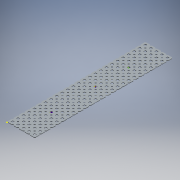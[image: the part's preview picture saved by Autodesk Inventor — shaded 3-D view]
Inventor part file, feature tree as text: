
AUTODESK INVENTOR PART (.ipt)
format: ipt  version: 2018 (Build 220112000, 112)  size: 2,300,416 bytes
history: native  units: mm (DEFAULTED — no unit token found)
features: other x125, extrude x125, sketch x4, imported_body x1, pattern_linear x1
ambient origin geometry x8: Origin, YZ Plane, XZ Plane, XY Plane, X Axis, Y Axis, Z Axis, Center Point
bodies: Solid1 (feature_tree)
feature tree (256):
  imported_body  "Base1"
  pattern_linear  "Rectangular Pattern1"  Count1=25  [1 undecoded]
  sketch  "Sketch2"  dims[d2=0.0mm d3=250.0mm]
  sketch  "Sketch3"  dims[d5=12.7mm d6=50.0mm d8=12.7mm]
  sketch  "Sketch4"  dims[d9=0.0mm d10=0.0mm d11=0.0mm d12=0.0mm d13=0.0mm d14=0.0mm d15=0.0mm d16=0.0mm d17=0.0mm d18=0.0mm d19=0.0mm d20=0.0mm d21=0.0mm d22=0.0mm d23=0.0mm d24=0.0mm d25=0.0mm d26=0.0mm d27=0.0mm d28=0.0mm d29=0.0mm d30=0.0mm d31=0.0mm d32=0.0mm d33=0.0mm d34=0.0mm d35=0.0mm d36=0.0mm d37=0.0mm d38=0.0mm d39=0.0mm d40=0.0mm d41=0.0mm d42=0.0mm d43=0.0mm d44=0.0mm d45=0.0mm d46=0.0mm d47=0.0mm d48=0.0mm d49=0.0mm d50=0.0mm d51=0.0mm d52=0.0mm d53=0.0mm d54=0.0mm d55=0.0mm d56=0.0mm d57=0.0mm d58=0.0mm d59=0.0mm d60=0.0mm d61=0.0mm d62=0.0mm d63=0.0mm d64=0.0mm d65=0.0mm d66=0.0mm d67=0.0mm d68=0.0mm d69=0.0mm d70=0.0mm d71=0.0mm d72=0.0mm d73=0.0mm d74=0.0mm d75=0.0mm d76=0.0mm d77=0.0mm d78=0.0mm d79=0.0mm d80=0.0mm d81=0.0mm d82=0.0mm d83=0.0mm d84=0.0mm d85=0.0mm d86=0.0mm d87=0.0mm d88=0.0mm d89=0.0mm d90=0.0mm d91=0.0mm d92=0.0mm d93=0.0mm d94=0.0mm d95=0.0mm d96=0.0mm d97=0.0mm d98=0.0mm d99=0.0mm d100=0.0mm d101=0.0mm d102=0.0mm d103=0.0mm d104=0.0mm d105=0.0mm d106=0.0mm d107=0.0mm d108=0.0mm d109=0.0mm d110=0.0mm d111=0.0mm d112=0.0mm d113=0.0mm d114=0.0mm d115=0.0mm d116=0.0mm d117=0.0mm d118=0.0mm d119=0.0mm d120=0.0mm d121=0.0mm d122=0.0mm d123=0.0mm d124=0.0mm d125=0.0mm d126=0.0mm d127=0.0mm d128=0.0mm d129=0.0mm d130=0.0mm d131=0.0mm d132=0.0mm d133=0.0mm d134=0.0mm d135=0.0mm d136=0.0mm d137=0.0mm d138=0.0mm d139=0.0mm d140=0.0mm d141=0.0mm d142=0.0mm d143=0.0mm d144=0.0mm d145=0.0mm d146=0.0mm d147=0.0mm d148=0.0mm d149=0.0mm d150=0.0mm d151=0.0mm d152=0.0mm d153=0.0mm d154=0.0mm d155=0.0mm d156=0.0mm d157=0.0mm d158=0.0mm d159=0.0mm d160=0.0mm d161=0.0mm d162=0.0mm d163=0.0mm d164=0.0mm d165=0.0mm d166=0.0mm d167=0.0mm d168=0.0mm d169=0.0mm d170=0.0mm d171=0.0mm d172=0.0mm d173=0.0mm d174=0.0mm d175=0.0mm d176=0.0mm d177=0.0mm d178=0.0mm d179=0.0mm d180=0.0mm d181=0.0mm d182=0.0mm d183=0.0mm d184=0.0mm d185=0.0mm d186=0.0mm d187=0.0mm d188=0.0mm d189=0.0mm d190=0.0mm d191=0.0mm d192=0.0mm d193=0.0mm d194=0.0mm d195=0.0mm d196=0.0mm d197=0.0mm d198=0.0mm d199=0.0mm d200=0.0mm d201=0.0mm d202=0.0mm d203=0.0mm d204=0.0mm d205=0.0mm d206=0.0mm d207=0.0mm d208=0.0mm d209=0.0mm d210=0.0mm d211=0.0mm d212=0.0mm d213=0.0mm d214=0.0mm d215=0.0mm d216=0.0mm d217=0.0mm d218=0.0mm d219=0.0mm d220=0.0mm d221=0.0mm d222=0.0mm d223=0.0mm d224=0.0mm d225=0.0mm d226=0.0mm d227=0.0mm d228=0.0mm d229=0.0mm d230=0.0mm d231=0.0mm d232=0.0mm d233=0.0mm d234=0.0mm d235=0.0mm d236=0.0mm d237=0.0mm d238=0.0mm d239=0.0mm d240=0.0mm d241=0.0mm d242=0.0mm d243=0.0mm d244=0.0mm d245=0.0mm d246=0.0mm d247=0.0mm d248=0.0mm d249=0.0mm d250=0.0mm d251=0.0mm d252=0.0mm d253=0.0mm d254=0.0mm d255=0.0mm d256=0.0mm d257=0.0mm d258=0.0mm]
  sketch  "Sketch1"  dims[d1=1.1684mm]
  other  "Srf1"
  other  "Srf2"
  other  "Srf3"
  other  "Srf4"
  other  "Srf5"
  other  "Srf6"
  other  "Srf7"
  other  "Srf8"
  other  "Srf9"
  other  "Srf10"
  other  "Srf11"
  other  "Srf12"
  other  "Srf13"
  other  "Srf14"
  other  "Srf15"
  other  "Srf16"
  other  "Srf17"
  other  "Srf18"
  other  "Srf19"
  other  "Srf20"
  other  "Srf21"
  other  "Srf22"
  other  "Srf23"
  other  "Srf24"
  other  "Srf25"
  other  "Srf26"
  other  "Srf27"
  other  "Srf28"
  other  "Srf29"
  other  "Srf30"
  other  "Srf31"
  other  "Srf32"
  other  "Srf33"
  other  "Srf34"
  other  "Srf35"
  other  "Srf36"
  other  "Srf37"
  other  "Srf38"
  other  "Srf39"
  other  "Srf40"
  other  "Srf41"
  other  "Srf42"
  other  "Srf43"
  other  "Srf44"
  other  "Srf45"
  other  "Srf46"
  other  "Srf47"
  other  "Srf48"
  other  "Srf49"
  other  "Srf50"
  other  "Srf51"
  other  "Srf52"
  other  "Srf53"
  other  "Srf54"
  other  "Srf55"
  other  "Srf56"
  other  "Srf57"
  other  "Srf58"
  other  "Srf59"
  other  "Srf60"
  other  "Srf61"
  other  "Srf62"
  other  "Srf63"
  other  "Srf64"
  other  "Srf65"
  other  "Srf66"
  other  "Srf67"
  other  "Srf68"
  other  "Srf69"
  other  "Srf70"
  other  "Srf71"
  other  "Srf72"
  other  "Srf73"
  other  "Srf74"
  other  "Srf75"
  other  "Srf76"
  other  "Srf77"
  other  "Srf78"
  other  "Srf79"
  other  "Srf80"
  other  "Srf81"
  other  "Srf82"
  other  "Srf83"
  other  "Srf84"
  other  "Srf85"
  other  "Srf86"
  other  "Srf87"
  other  "Srf88"
  other  "Srf89"
  other  "Srf90"
  other  "Srf91"
  other  "Srf92"
  other  "Srf93"
  other  "Srf94"
  other  "Srf95"
  other  "Srf96"
  other  "Srf97"
  other  "Srf98"
  other  "Srf99"
  other  "Srf100"
  other  "Srf101"
  other  "Srf102"
  other  "Srf103"
  other  "Srf104"
  other  "Srf105"
  other  "Srf106"
  other  "Srf107"
  other  "Srf108"
  other  "Srf109"
  other  "Srf110"
  other  "Srf111"
  other  "Srf112"
  other  "Srf113"
  other  "Srf114"
  other  "Srf115"
  other  "Srf116"
  other  "Srf117"
  other  "Srf118"
  other  "Srf119"
  other  "Srf120"
  other  "Srf121"
  other  "Srf122"
  other  "Srf123"
  other  "Srf124"
  other  "Srf125"
  extrude  "ExtrusionSrf1"  Depth=50.0mm
  extrude  "ExtrusionSrf2"  TaperAngle=0.0deg  [1 undecoded]
  extrude  "ExtrusionSrf3"  TaperAngle=0.0deg  [1 undecoded]
  extrude  "ExtrusionSrf4"  TaperAngle=0.0deg  [1 undecoded]
  extrude  "ExtrusionSrf5"  TaperAngle=0.0deg  [1 undecoded]
  extrude  "ExtrusionSrf6"  TaperAngle=0.0deg  [1 undecoded]
  extrude  "ExtrusionSrf7"  TaperAngle=0.0deg  [1 undecoded]
  extrude  "ExtrusionSrf8"  TaperAngle=0.0deg  [1 undecoded]
  extrude  "ExtrusionSrf9"  TaperAngle=0.0deg  [1 undecoded]
  extrude  "ExtrusionSrf10"  TaperAngle=0.0deg  [1 undecoded]
  extrude  "ExtrusionSrf11"  TaperAngle=0.0deg  [1 undecoded]
  extrude  "ExtrusionSrf12"  TaperAngle=0.0deg  [1 undecoded]
  extrude  "ExtrusionSrf13"  TaperAngle=0.0deg  [1 undecoded]
  extrude  "ExtrusionSrf14"  TaperAngle=0.0deg  [1 undecoded]
  extrude  "ExtrusionSrf15"  TaperAngle=0.0deg  [1 undecoded]
  extrude  "ExtrusionSrf16"  TaperAngle=0.0deg  [1 undecoded]
  extrude  "ExtrusionSrf17"  TaperAngle=0.0deg  [1 undecoded]
  extrude  "ExtrusionSrf18"  TaperAngle=0.0deg  [1 undecoded]
  extrude  "ExtrusionSrf19"  TaperAngle=0.0deg  [1 undecoded]
  extrude  "ExtrusionSrf20"  TaperAngle=0.0deg  [1 undecoded]
  extrude  "ExtrusionSrf21"  TaperAngle=0.0deg  [1 undecoded]
  extrude  "ExtrusionSrf22"  TaperAngle=0.0deg  [1 undecoded]
  extrude  "ExtrusionSrf23"  TaperAngle=0.0deg  [1 undecoded]
  extrude  "ExtrusionSrf24"  TaperAngle=0.0deg  [1 undecoded]
  extrude  "ExtrusionSrf25"  TaperAngle=0.0deg  [1 undecoded]
  extrude  "ExtrusionSrf26"  TaperAngle=0.0deg  [1 undecoded]
  extrude  "ExtrusionSrf27"  TaperAngle=0.0deg  [1 undecoded]
  extrude  "ExtrusionSrf28"  TaperAngle=0.0deg  [1 undecoded]
  extrude  "ExtrusionSrf29"  TaperAngle=0.0deg  [1 undecoded]
  extrude  "ExtrusionSrf30"  TaperAngle=0.0deg  [1 undecoded]
  extrude  "ExtrusionSrf31"  TaperAngle=0.0deg  [1 undecoded]
  extrude  "ExtrusionSrf32"  TaperAngle=0.0deg  [1 undecoded]
  extrude  "ExtrusionSrf33"  TaperAngle=0.0deg  [1 undecoded]
  extrude  "ExtrusionSrf34"  TaperAngle=0.0deg  [1 undecoded]
  extrude  "ExtrusionSrf35"  TaperAngle=0.0deg  [1 undecoded]
  extrude  "ExtrusionSrf36"  TaperAngle=0.0deg  [1 undecoded]
  extrude  "ExtrusionSrf37"  TaperAngle=0.0deg  [1 undecoded]
  extrude  "ExtrusionSrf38"  TaperAngle=0.0deg  [1 undecoded]
  extrude  "ExtrusionSrf39"  TaperAngle=0.0deg  [1 undecoded]
  extrude  "ExtrusionSrf40"  TaperAngle=0.0deg  [1 undecoded]
  extrude  "ExtrusionSrf41"  TaperAngle=0.0deg  [1 undecoded]
  extrude  "ExtrusionSrf42"  TaperAngle=0.0deg  [1 undecoded]
  extrude  "ExtrusionSrf43"  TaperAngle=0.0deg  [1 undecoded]
  extrude  "ExtrusionSrf44"  TaperAngle=0.0deg  [1 undecoded]
  extrude  "ExtrusionSrf45"  TaperAngle=0.0deg  [1 undecoded]
  extrude  "ExtrusionSrf46"  TaperAngle=0.0deg  [1 undecoded]
  extrude  "ExtrusionSrf47"  TaperAngle=0.0deg  [1 undecoded]
  extrude  "ExtrusionSrf48"  TaperAngle=0.0deg  [1 undecoded]
  extrude  "ExtrusionSrf49"  TaperAngle=0.0deg  [1 undecoded]
  extrude  "ExtrusionSrf50"  TaperAngle=0.0deg  [1 undecoded]
  extrude  "ExtrusionSrf51"  TaperAngle=0.0deg  [1 undecoded]
  extrude  "ExtrusionSrf52"  TaperAngle=0.0deg  [1 undecoded]
  extrude  "ExtrusionSrf53"  TaperAngle=0.0deg  [1 undecoded]
  extrude  "ExtrusionSrf54"  TaperAngle=0.0deg  [1 undecoded]
  extrude  "ExtrusionSrf55"  TaperAngle=0.0deg  [1 undecoded]
  extrude  "ExtrusionSrf56"  TaperAngle=0.0deg  [1 undecoded]
  extrude  "ExtrusionSrf57"  TaperAngle=0.0deg  [1 undecoded]
  extrude  "ExtrusionSrf58"  TaperAngle=0.0deg  [1 undecoded]
  extrude  "ExtrusionSrf59"  TaperAngle=0.0deg  [1 undecoded]
  extrude  "ExtrusionSrf60"  TaperAngle=0.0deg  [1 undecoded]
  extrude  "ExtrusionSrf61"  TaperAngle=0.0deg  [1 undecoded]
  extrude  "ExtrusionSrf62"  TaperAngle=0.0deg  [1 undecoded]
  extrude  "ExtrusionSrf63"  TaperAngle=0.0deg  [1 undecoded]
  extrude  "ExtrusionSrf64"  TaperAngle=0.0deg  [1 undecoded]
  extrude  "ExtrusionSrf65"  TaperAngle=0.0deg  [1 undecoded]
  extrude  "ExtrusionSrf66"  TaperAngle=0.0deg  [1 undecoded]
  extrude  "ExtrusionSrf67"  TaperAngle=0.0deg  [1 undecoded]
  extrude  "ExtrusionSrf68"  TaperAngle=0.0deg  [1 undecoded]
  extrude  "ExtrusionSrf69"  TaperAngle=0.0deg  [1 undecoded]
  extrude  "ExtrusionSrf70"  TaperAngle=0.0deg  [1 undecoded]
  extrude  "ExtrusionSrf71"  TaperAngle=0.0deg  [1 undecoded]
  extrude  "ExtrusionSrf72"  TaperAngle=0.0deg  [1 undecoded]
  extrude  "ExtrusionSrf73"  TaperAngle=0.0deg  [1 undecoded]
  extrude  "ExtrusionSrf74"  TaperAngle=0.0deg  [1 undecoded]
  extrude  "ExtrusionSrf75"  TaperAngle=0.0deg  [1 undecoded]
  extrude  "ExtrusionSrf76"  TaperAngle=0.0deg  [1 undecoded]
  extrude  "ExtrusionSrf77"  TaperAngle=0.0deg  [1 undecoded]
  extrude  "ExtrusionSrf78"  TaperAngle=0.0deg  [1 undecoded]
  extrude  "ExtrusionSrf79"  TaperAngle=0.0deg  [1 undecoded]
  extrude  "ExtrusionSrf80"  TaperAngle=0.0deg  [1 undecoded]
  extrude  "ExtrusionSrf81"  TaperAngle=0.0deg  [1 undecoded]
  extrude  "ExtrusionSrf82"  TaperAngle=0.0deg  [1 undecoded]
  extrude  "ExtrusionSrf83"  TaperAngle=0.0deg  [1 undecoded]
  extrude  "ExtrusionSrf84"  TaperAngle=0.0deg  [1 undecoded]
  extrude  "ExtrusionSrf85"  TaperAngle=0.0deg  [1 undecoded]
  extrude  "ExtrusionSrf86"  TaperAngle=0.0deg  [1 undecoded]
  extrude  "ExtrusionSrf87"  TaperAngle=0.0deg  [1 undecoded]
  extrude  "ExtrusionSrf88"  TaperAngle=0.0deg  [1 undecoded]
  extrude  "ExtrusionSrf89"  TaperAngle=0.0deg  [1 undecoded]
  extrude  "ExtrusionSrf90"  TaperAngle=0.0deg  [1 undecoded]
  extrude  "ExtrusionSrf91"  TaperAngle=0.0deg  [1 undecoded]
  extrude  "ExtrusionSrf92"  TaperAngle=0.0deg  [1 undecoded]
  extrude  "ExtrusionSrf93"  TaperAngle=0.0deg  [1 undecoded]
  extrude  "ExtrusionSrf94"  TaperAngle=0.0deg  [1 undecoded]
  extrude  "ExtrusionSrf95"  TaperAngle=0.0deg  [1 undecoded]
  extrude  "ExtrusionSrf96"  TaperAngle=0.0deg  [1 undecoded]
  extrude  "ExtrusionSrf97"  TaperAngle=0.0deg  [1 undecoded]
  extrude  "ExtrusionSrf98"  TaperAngle=0.0deg  [1 undecoded]
  extrude  "ExtrusionSrf99"  TaperAngle=0.0deg  [1 undecoded]
  extrude  "ExtrusionSrf100"  TaperAngle=0.0deg  [1 undecoded]
  extrude  "ExtrusionSrf101"  TaperAngle=0.0deg  [1 undecoded]
  extrude  "ExtrusionSrf102"  TaperAngle=0.0deg  [1 undecoded]
  extrude  "ExtrusionSrf103"  TaperAngle=0.0deg  [1 undecoded]
  extrude  "ExtrusionSrf104"  TaperAngle=0.0deg  [1 undecoded]
  extrude  "ExtrusionSrf105"  TaperAngle=0.0deg  [1 undecoded]
  extrude  "ExtrusionSrf106"  TaperAngle=0.0deg  [1 undecoded]
  extrude  "ExtrusionSrf107"  TaperAngle=0.0deg  [1 undecoded]
  extrude  "ExtrusionSrf108"  TaperAngle=0.0deg  [1 undecoded]
  extrude  "ExtrusionSrf109"  TaperAngle=0.0deg  [1 undecoded]
  extrude  "ExtrusionSrf110"  TaperAngle=0.0deg  [1 undecoded]
  extrude  "ExtrusionSrf111"  TaperAngle=0.0deg  [1 undecoded]
  extrude  "ExtrusionSrf112"  TaperAngle=0.0deg  [1 undecoded]
  extrude  "ExtrusionSrf113"  TaperAngle=0.0deg  [1 undecoded]
  extrude  "ExtrusionSrf114"  TaperAngle=0.0deg  [1 undecoded]
  extrude  "ExtrusionSrf115"  TaperAngle=0.0deg  [1 undecoded]
  extrude  "ExtrusionSrf116"  TaperAngle=0.0deg  [1 undecoded]
  extrude  "ExtrusionSrf117"  TaperAngle=0.0deg  [1 undecoded]
  extrude  "ExtrusionSrf118"  TaperAngle=0.0deg  [1 undecoded]
  extrude  "ExtrusionSrf119"  TaperAngle=0.0deg  [1 undecoded]
  extrude  "ExtrusionSrf120"  TaperAngle=0.0deg  [1 undecoded]
  extrude  "ExtrusionSrf121"  TaperAngle=0.0deg  [1 undecoded]
  extrude  "ExtrusionSrf122"  TaperAngle=0.0deg  [1 undecoded]
  extrude  "ExtrusionSrf123"  TaperAngle=0.0deg  [1 undecoded]
  extrude  "ExtrusionSrf124"  TaperAngle=0.0deg  [1 undecoded]
  extrude  "ExtrusionSrf125"  TaperAngle=0.0deg  [1 undecoded]
note: 125 required parameter values undecoded (feature->parameter linkage not recoverable at this tier; creation-order binding heuristic only, values carry confidence <= 0.55)
